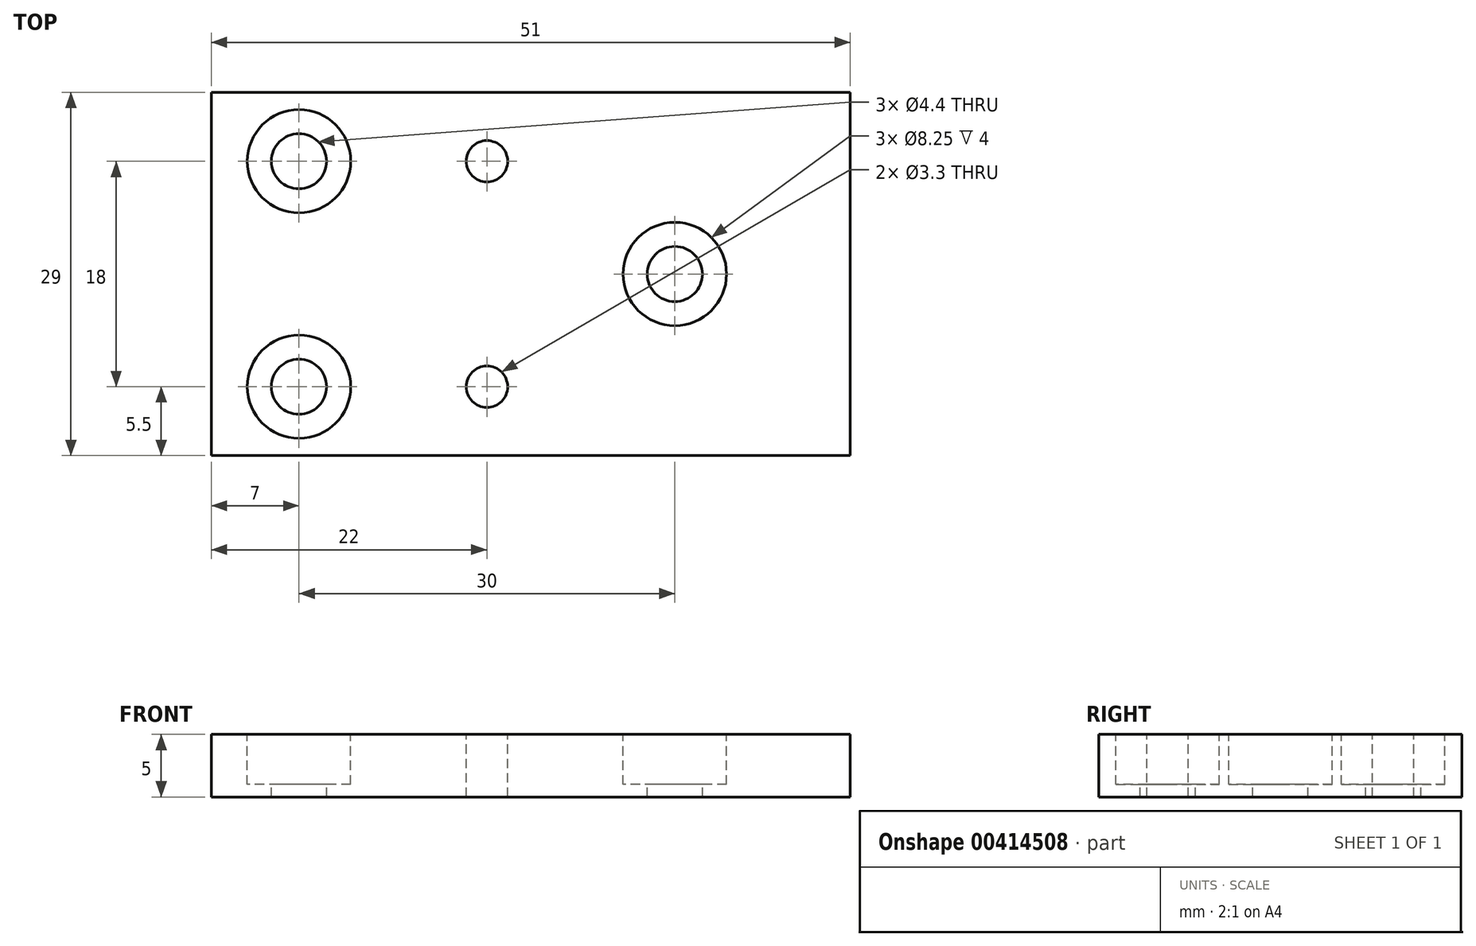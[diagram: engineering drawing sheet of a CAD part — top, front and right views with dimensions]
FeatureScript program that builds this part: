
annotation { "Feature Type Name" : "Feature", "Feature Type Description" : "" }
export const myFeature = defineFeature(function(context is Context, id is Id, definition is map)
    precondition{}
    {
        {
            var Q0;
            Q0=qCreatedBy(makeId("Top.planeOp"),FACE);
            var sketch = newSketch(context, id + "F0", { "sketchPlane" : qUnion([Q0])});
            skLineSegment(sketch, "E0.bottom", {"start": v(-25.5, -14.5) * mm, "end": v(25.5, -14.5) * mm});
            skLineSegment(sketch, "E0.top", {"start": v(-25.5, 14.5) * mm, "end": v(25.5, 14.5) * mm});
            skLineSegment(sketch, "E0.left", {"start": v(-25.5, -14.5) * mm, "end": v(-25.5, 14.5) * mm});
            skLineSegment(sketch, "E0.right", {"start": v(25.5, -14.5) * mm, "end": v(25.5, 14.5) * mm});
            skPoint(sketch, "E0.middle", {"position": v(0, 0) * mm});
            skSolve(sketch);
        }
        {
            var Q0;
            Q0 = qSketchRegion(id + "F0", true);
            extrude(context, id + "F1", {"entities" : qUnion([Q0]), "depth" : 5 * mm});
        }
        {
            var Q0;
            Q0=makeQuery(id+"F1.opExtrude","CAP_FACE",FACE,{"disambiguationData":[OSD([sQuery(id+"F0.wireOp",EDGE,"E0.bottom"),sQuery(id+"F0.wireOp",EDGE,"E0.top"),sQuery(id+"F0.wireOp",EDGE,"E0.left"),sQuery(id+"F0.wireOp",EDGE,"E0.right")])],"isStart":false});
            var sketch = newSketch(context, id + "F2", { "sketchPlane" : qUnion([Q0])});
            skLineSegment(sketch, "E1", {"start": v(-18.5, 9) * mm, "end": v(-18.5, -9) * mm, "construction": true});
            skPoint(sketch, "E2", {"position": v(-18.5, 9) * mm});
            skPoint(sketch, "E3", {"position": v(-18.5, -9) * mm});
            skPoint(sketch, "E4", {"position": v(11.5, 0) * mm});
            skSolve(sketch);
        }
        {
            var Q0;
            Q0=sQuery(id+"F2.wireOp",VERTEX,"E2");
            var Q1;
            Q1=sQuery(id+"F2.wireOp",VERTEX,"E3");
            var Q2;
            Q2=sQuery(id+"F2.wireOp",VERTEX,"E4");
            var Q3;
            Q3=makeQuery(id+"F1.opExtrude","SWEPT_BODY",BODY,{"disambiguationData":[OSD([sQuery(id+"F0.wireOp",EDGE,"E0.bottom"),sQuery(id+"F0.wireOp",EDGE,"E0.top"),sQuery(id+"F0.wireOp",EDGE,"E0.left"),sQuery(id+"F0.wireOp",EDGE,"E0.right")])]});
            hole(context, id + "F3", {"style" : HoleStyle.C_BORE, "endStyle" : HoleEndStyle.BLIND, "standardTappedOrClearance" : lookupTablePath({ "standard" : "ISO", "fit" : "Normal", "size" : "M4", "type" : "Clearance" }), "standardBlindInLast" : lookupTablePath({ "fit" : "Standard", "standard" : "ISO", "size" : "M4", "type" : "Clearance" }), "holeDiameter" : 4.4 * mm, "cBoreDiameter" : 8.25 * mm, "cBoreDepth" : 4 * mm, "holeDepth" : 6 * mm, "tappedDepth" : 5 * mm, "tapClearance" : 2, "startFromSketch" : true, "locations" : qUnion([Q0, Q1, Q2]), "scope" : qUnion([Q3])});
        }
        {
            var Q0;
            Q0=makeQuery(id+"F1.opExtrude","CAP_FACE",FACE,{"disambiguationData":[OSD([sQuery(id+"F0.wireOp",EDGE,"E0.bottom"),sQuery(id+"F0.wireOp",EDGE,"E0.top"),sQuery(id+"F0.wireOp",EDGE,"E0.left"),sQuery(id+"F0.wireOp",EDGE,"E0.right")])],"isStart":false});
            var sketch = newSketch(context, id + "F4", { "sketchPlane" : qUnion([Q0])});
            skLineSegment(sketch, "E5", {"start": v(-3.5, 9) * mm, "end": v(-3.5, -9) * mm, "construction": true});
            skPoint(sketch, "E6", {"position": v(-3.5, 9) * mm});
            skPoint(sketch, "E7", {"position": v(-3.5, -9) * mm});
            skSolve(sketch);
        }
        {
            var Q0;
            Q0=sQuery(id+"F4.wireOp",VERTEX,"E6");
            var Q1;
            Q1=sQuery(id+"F4.wireOp",VERTEX,"E7");
            var Q2;
            Q2=makeQuery(id+"F1.opExtrude","SWEPT_BODY",BODY,{"disambiguationData":[OSD([sQuery(id+"F0.wireOp",EDGE,"E0.bottom"),sQuery(id+"F0.wireOp",EDGE,"E0.top"),sQuery(id+"F0.wireOp",EDGE,"E0.left"),sQuery(id+"F0.wireOp",EDGE,"E0.right")])]});
            hole(context, id + "F5", {"style" : HoleStyle.SIMPLE, "endStyle" : HoleEndStyle.THROUGH, "standardTappedOrClearance" : lookupTablePath({ "standard" : "ISO", "engagement" : "75%", "pitch" : "0.7 mm", "size" : "M4", "type" : "Tapped" }), "standardBlindInLast" : lookupTablePath({ "standard" : "ISO", "engagement" : "75%", "pitch" : "0.7 mm", "size" : "M4", "type" : "Tapped" }), "holeDiameter" : 3.3 * mm, "showTappedDepth" : true, "isTappedThrough" : true, "tappedDepth" : 5 * mm, "tapClearance" : 2, "startFromSketch" : true, "locations" : qUnion([Q0, Q1]), "scope" : qUnion([Q2]), "majorDiameter" : 4 * mm});
        }
    });
